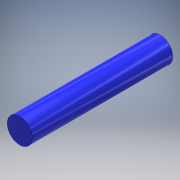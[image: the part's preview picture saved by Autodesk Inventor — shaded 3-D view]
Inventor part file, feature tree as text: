
AUTODESK INVENTOR PART (.ipt)
format: ipt  version: 2017 (Build 210142000, 142)  size: 99,840 bytes
history: native  units: mm
features: extrude x1, sketch x1
ambient origin geometry x8: Origin, YZ Plane, XZ Plane, XY Plane, X Axis, Y Axis, Z Axis, Center Point
bodies: Solid1 (feature_tree)
feature tree (2):
  extrude  "Extrusion1"  Depth=45.0mm TaperAngle=0.0deg
  sketch  "Sketch1"  dims[d0=8.0mm d1=45.0mm d2=0.0mm]
